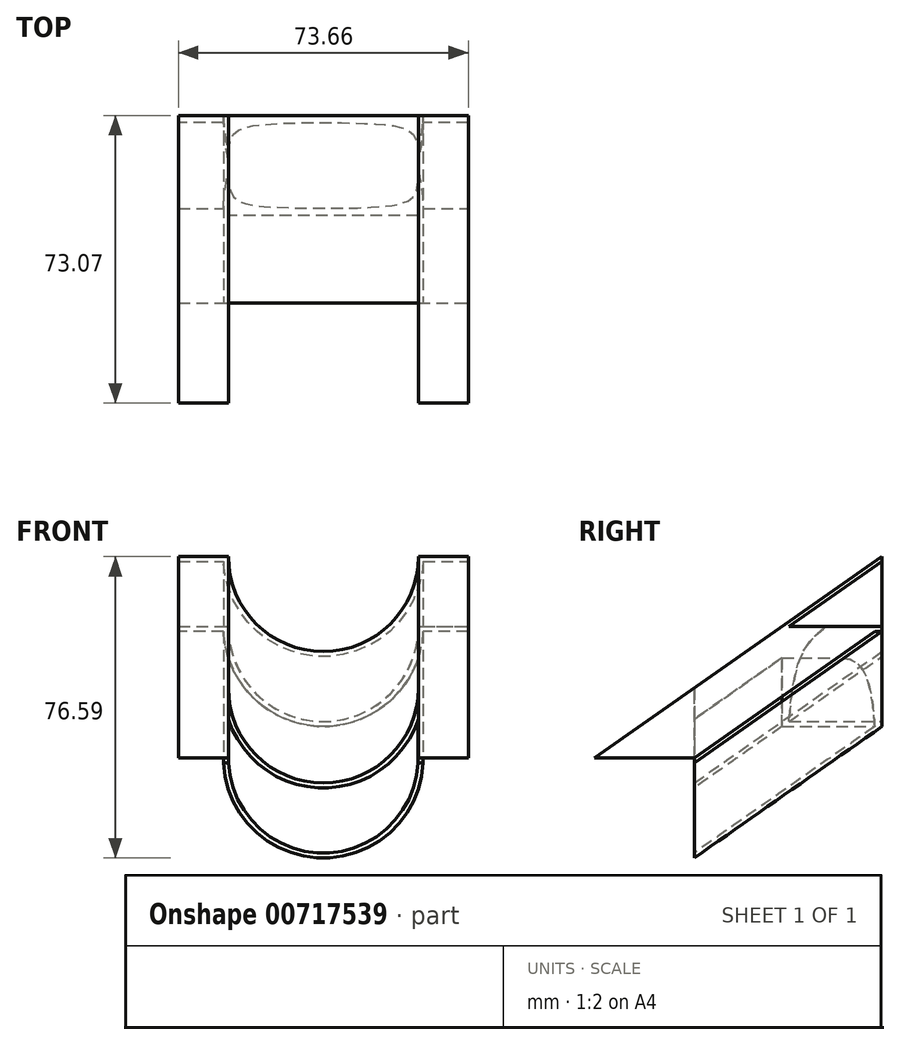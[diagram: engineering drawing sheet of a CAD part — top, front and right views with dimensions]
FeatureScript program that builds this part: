
annotation { "Feature Type Name" : "Feature", "Feature Type Description" : "" }
export const myFeature = defineFeature(function(context is Context, id is Id, definition is map)
    precondition{}
    {
        {
            var Q0;
            Q0=qCreatedBy(makeId("Front.planeOp"),FACE);
            var sketch = newSketch(context, id + "F0", { "sketchPlane" : qUnion([Q0])});
            skArc(sketch, "E0", {"start": v(-25.4, 0) * mm, "mid": v(0, -25.4) * mm, "end": v(25.4, 0) * mm});
            skLineSegment(sketch, "E1.bottom", {"start": v(-36.83, 0) * mm, "end": v(-24.13, 0) * mm});
            skLineSegment(sketch, "E1.top", {"start": v(-36.83, -1.27) * mm, "end": v(-24.1, -1.27) * mm});
            skLineSegment(sketch, "E1.left", {"start": v(-36.83, 0) * mm, "end": v(-36.83, -1.27) * mm});
            skLineSegment(sketch, "E1.right", {"start": v(36.83, 0) * mm, "end": v(36.83, -1.27) * mm});
            skArc(sketch, "E2", {"start": v(-24.13, 0) * mm, "mid": v(0, -24.13) * mm, "end": v(24.13, 0) * mm});
            skLineSegment(sketch, "E3.trimOffspring", {"start": v(24.13, 0) * mm, "end": v(36.83, 0) * mm});
            skLineSegment(sketch, "E4", {"start": v(0, -24.13) * mm, "end": v(0, -25.4) * mm, "construction": true});
            skLineSegment(sketch, "E5.trimOffspring", {"start": v(24.1, -1.27) * mm, "end": v(36.83, -1.27) * mm});
            skSolve(sketch);
        }
        {
            var Q0;
            Q0 = qSketchRegion(id + "F0", true);
            extrude(context, id + "F1", {"entities" : qUnion([Q0]), "depth" : 25.4 * mm, "offsetDistance" : 25.4 * mm});
        }
        {
            var Q0;
            Q0=qCreatedBy(makeId("Right.planeOp"),FACE);
            var sketch = newSketch(context, id + "F2", { "sketchPlane" : qUnion([Q0])});
            skLineSegment(sketch, "E6", {"start": v(0, 0) * mm, "end": v(-47.67, -33.4) * mm});
            skSolve(sketch);
        }
        {
            var Q0;
            Q0=makeQuery(id+"F1.opExtrude","SWEPT_FACE",FACE,{"disambiguationData":[OSD([sQuery(id+"F0.wireOp",EDGE,"E1.bottom")])]});
            var Q1;
            Q1=makeQuery(id+"F1.opExtrude","CAP_FACE",FACE,{"disambiguationData":[OSD([sQuery(id+"F0.wireOp",EDGE,"E0"),sQuery(id+"F0.wireOp",EDGE,"E1.bottom"),sQuery(id+"F0.wireOp",EDGE,"E1.top"),sQuery(id+"F0.wireOp",EDGE,"E1.left"),sQuery(id+"F0.wireOp",EDGE,"E1.right"),sQuery(id+"F0.wireOp",EDGE,"E2"),sQuery(id+"F0.wireOp",EDGE,"E3.trimOffspring"),sQuery(id+"F0.wireOp",EDGE,"E5.trimOffspring")])],"isStart":false});
            var Q2;
            Q2=makeQuery(id+"F1.opExtrude","SWEPT_FACE",FACE,{"disambiguationData":[OSD([sQuery(id+"F0.wireOp",EDGE,"E3.trimOffspring")])]});
            var Q3;
            {var subQ0=sQuery(id+"F0.wireOp",EDGE,"E1.top");var subQ1=sQuery(id+"F0.wireOp",EDGE,"E0");var subQ2=makeQuery(id+"F0.imprint","INTERSECT",VERTEX,{"derivedFrom":[subQ1,subQ0]});Q3=makeQuery(id+"F0.imprint","IMPRINT",FACE,{"disambiguationData":[TD([[makeQuery(id+"F0.imprint","IMPRINT",EDGE,{"disambiguationData":[TD([[subQ2,-1.0]])],"derivedFrom":subQ1}),1.0]])]});}
            var Q4;
            Q4=sQuery(id+"F2.wireOp",EDGE,"E6");
            sweep(context, id + "F3", {"operationType" : NewBodyOperationType.ADD, "profiles" : qUnion([Q0, Q1, Q2, Q3]), "path" : qUnion([Q4])});
        }
    });
